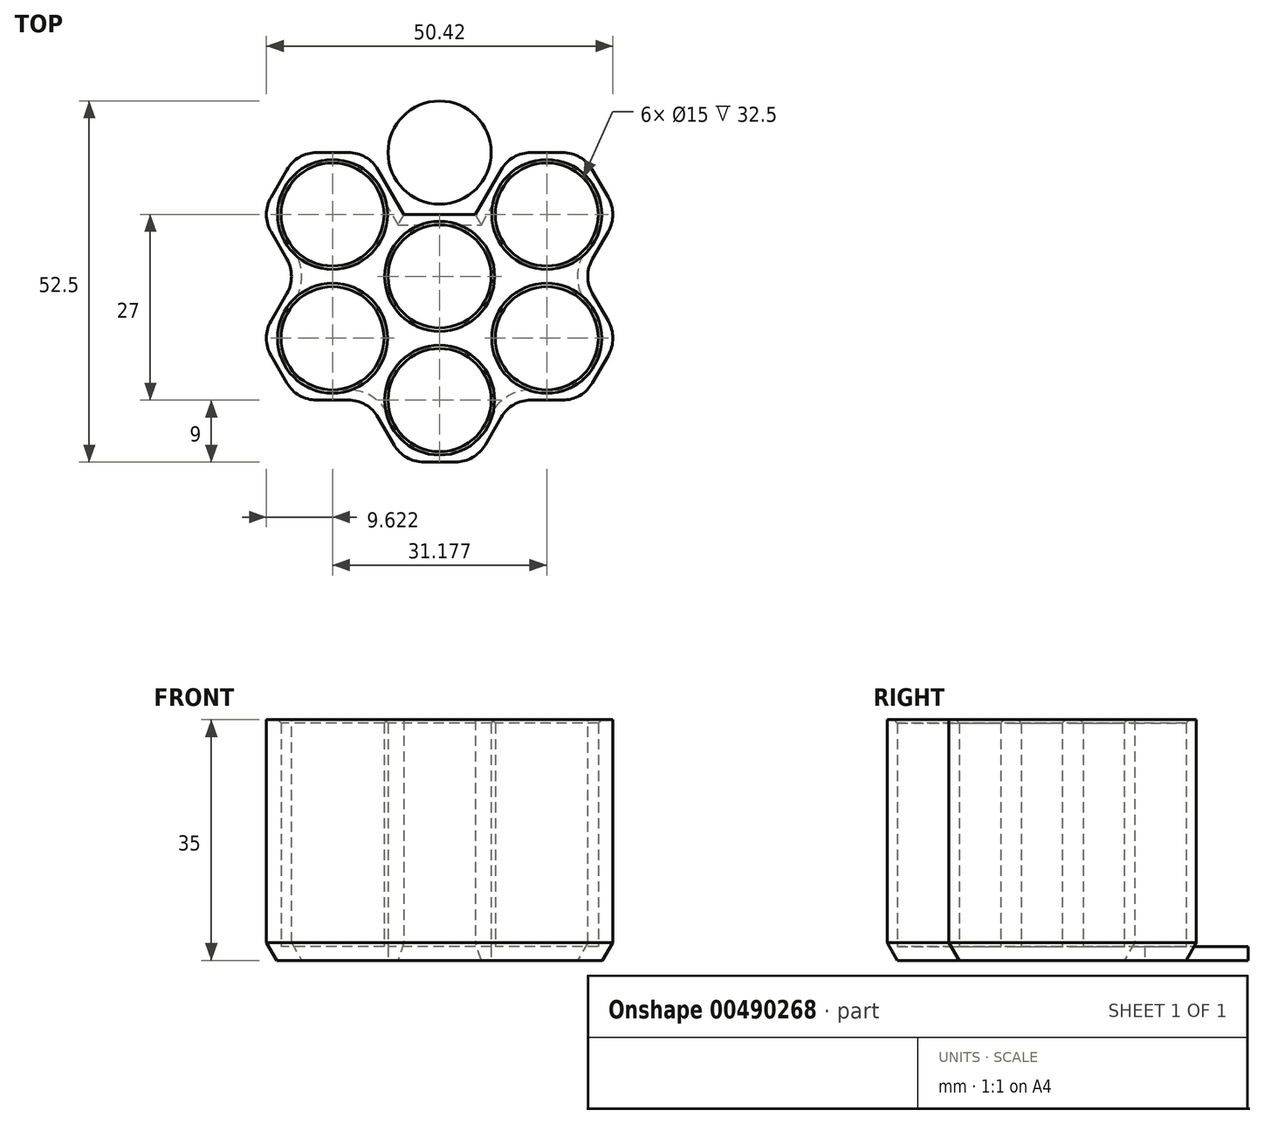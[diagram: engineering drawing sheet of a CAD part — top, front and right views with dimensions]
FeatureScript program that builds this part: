
annotation { "Feature Type Name" : "Feature", "Feature Type Description" : "" }
export const myFeature = defineFeature(function(context is Context, id is Id, definition is map)
    precondition{}
    {
        {
            var Q0;
            Q0=qCreatedBy(makeId("Top.planeOp"),FACE);
            var sketch = newSketch(context, id + "F0", { "sketchPlane" : qUnion([Q0])});
            skCircle(sketch, "E0", {"center": v(0, 0) * mm, "radius": 7.5 * mm});
            skCircle(sketch, "E1.cCircle", {"center": v(0, 0) * mm, "radius": 9 * mm, "construction": true});
            skLineSegment(sketch, "E1.0", {"start": v(-5.2, 9) * mm, "end": v(5.2, 9) * mm});
            skLineSegment(sketch, "E1.1", {"start": v(5.2, 9) * mm, "end": v(10.4, 0) * mm});
            skLineSegment(sketch, "E1.2", {"start": v(10.4, 0) * mm, "end": v(5.2, -9) * mm});
            skLineSegment(sketch, "E1.3", {"start": v(5.2, -9) * mm, "end": v(-5.2, -9) * mm});
            skLineSegment(sketch, "E1.4", {"start": v(-5.2, -9) * mm, "end": v(-10.4, 0) * mm});
            skLineSegment(sketch, "E1.5", {"start": v(-10.4, 0) * mm, "end": v(-5.2, 9) * mm});
            skPoint(sketch, "E1.0.midPoint", {"position": v(0, 9) * mm});
            skCircle(sketch, "E2.cCircle", {"center": v(0, 18) * mm, "radius": 9 * mm, "construction": true});
            skLineSegment(sketch, "E2.0", {"start": v(5.2, 9) * mm, "end": v(-5.2, 9) * mm});
            skLineSegment(sketch, "E2.1", {"start": v(-5.2, 9) * mm, "end": v(-10.4, 18) * mm});
            skLineSegment(sketch, "E2.2", {"start": v(-10.4, 18) * mm, "end": v(-5.2, 27) * mm});
            skLineSegment(sketch, "E2.3", {"start": v(-5.2, 27) * mm, "end": v(5.2, 27) * mm});
            skLineSegment(sketch, "E2.4", {"start": v(5.2, 27) * mm, "end": v(10.4, 18) * mm});
            skLineSegment(sketch, "E2.5", {"start": v(10.4, 18) * mm, "end": v(5.2, 9) * mm});
            skLineSegment(sketch, "E3.1.0", {"start": v(-25.98, 9) * mm, "end": v(-20.78, 18) * mm});
            skLineSegment(sketch, "E3.1.1", {"start": v(-20.78, 18) * mm, "end": v(-10.4, 18) * mm});
            skLineSegment(sketch, "E3.1.2", {"start": v(-10.4, 18) * mm, "end": v(-5.2, 9) * mm});
            skLineSegment(sketch, "E3.1.3", {"start": v(-10.4, 0) * mm, "end": v(-20.78, 0) * mm});
            skLineSegment(sketch, "E3.1.4", {"start": v(-20.78, 0) * mm, "end": v(-25.98, 9) * mm});
            skLineSegment(sketch, "E3.2.0", {"start": v(-20.78, -18) * mm, "end": v(-25.98, -9) * mm});
            skLineSegment(sketch, "E3.2.1", {"start": v(-25.98, -9) * mm, "end": v(-20.78, 0) * mm});
            skLineSegment(sketch, "E3.2.2", {"start": v(-20.78, 0) * mm, "end": v(-10.4, 0) * mm});
            skLineSegment(sketch, "E3.2.3", {"start": v(-5.2, -9) * mm, "end": v(-10.4, -18) * mm});
            skLineSegment(sketch, "E3.2.4", {"start": v(-10.4, -18) * mm, "end": v(-20.78, -18) * mm});
            skLineSegment(sketch, "E3.3.0", {"start": v(5.2, -27) * mm, "end": v(-5.2, -27) * mm});
            skLineSegment(sketch, "E3.3.1", {"start": v(-5.2, -27) * mm, "end": v(-10.4, -18) * mm});
            skLineSegment(sketch, "E3.3.2", {"start": v(-10.4, -18) * mm, "end": v(-5.2, -9) * mm});
            skLineSegment(sketch, "E3.3.3", {"start": v(5.2, -9) * mm, "end": v(10.4, -18) * mm});
            skLineSegment(sketch, "E3.3.4", {"start": v(10.4, -18) * mm, "end": v(5.2, -27) * mm});
            skLineSegment(sketch, "E3.4.0", {"start": v(25.98, -9) * mm, "end": v(20.78, -18) * mm});
            skLineSegment(sketch, "E3.4.1", {"start": v(20.78, -18) * mm, "end": v(10.4, -18) * mm});
            skLineSegment(sketch, "E3.4.2", {"start": v(10.4, -18) * mm, "end": v(5.2, -9) * mm});
            skLineSegment(sketch, "E3.4.3", {"start": v(10.4, 0) * mm, "end": v(20.78, 0) * mm});
            skLineSegment(sketch, "E3.4.4", {"start": v(20.78, 0) * mm, "end": v(25.98, -9) * mm});
            skLineSegment(sketch, "E3.5.0", {"start": v(20.78, 18) * mm, "end": v(25.98, 9) * mm});
            skLineSegment(sketch, "E3.5.1", {"start": v(25.98, 9) * mm, "end": v(20.78, 0) * mm});
            skLineSegment(sketch, "E3.5.2", {"start": v(20.78, 0) * mm, "end": v(10.4, 0) * mm});
            skLineSegment(sketch, "E3.5.3", {"start": v(5.2, 9) * mm, "end": v(10.4, 18) * mm});
            skLineSegment(sketch, "E3.5.4", {"start": v(10.4, 18) * mm, "end": v(20.78, 18) * mm});
            skCircle(sketch, "E4", {"center": v(0, 18) * mm, "radius": 7.5 * mm});
            skCircle(sketch, "E5.1.0", {"center": v(-15.59, 9) * mm, "radius": 7.5 * mm});
            skCircle(sketch, "E5.2.0", {"center": v(-15.59, -9) * mm, "radius": 7.5 * mm});
            skCircle(sketch, "E5.3.0", {"center": v(0, -18) * mm, "radius": 7.5 * mm});
            skCircle(sketch, "E5.4.0", {"center": v(15.59, -9) * mm, "radius": 7.5 * mm});
            skCircle(sketch, "E5.5.0", {"center": v(15.59, 9) * mm, "radius": 7.5 * mm});
            skSolve(sketch);
        }
        {
            var Q0;
            Q0=makeQuery(id+"F0.imprint","IMPRINT",FACE,{"disambiguationData":[TD([[makeQuery(id+"F0.imprint","IMPRINT",EDGE,{"derivedFrom":sQuery(id+"F0.wireOp",EDGE,"E1.5")}),1.0]])]});
            var Q1;
            Q1=makeQuery(id+"F0.imprint","IMPRINT",FACE,{"disambiguationData":[TD([[makeQuery(id+"F0.imprint","IMPRINT",EDGE,{"derivedFrom":sQuery(id+"F0.wireOp",EDGE,"E2.0")}),-1.0]])]});
            var Q2;
            Q2=makeQuery(id+"F0.imprint","IMPRINT",FACE,{"disambiguationData":[TD([[makeQuery(id+"F0.imprint","IMPRINT",EDGE,{"derivedFrom":sQuery(id+"F0.wireOp",EDGE,"E1.1")}),1.0]])]});
            var Q3;
            Q3=makeQuery(id+"F0.imprint","IMPRINT",FACE,{"disambiguationData":[TD([[makeQuery(id+"F0.imprint","IMPRINT",EDGE,{"derivedFrom":sQuery(id+"F0.wireOp",EDGE,"E0")}),-1.0]])]});
            var Q4;
            Q4=makeQuery(id+"F0.imprint","IMPRINT",FACE,{"disambiguationData":[TD([[makeQuery(id+"F0.imprint","IMPRINT",EDGE,{"derivedFrom":sQuery(id+"F0.wireOp",EDGE,"E1.2")}),1.0]])]});
            var Q5;
            Q5=makeQuery(id+"F0.imprint","IMPRINT",FACE,{"disambiguationData":[TD([[makeQuery(id+"F0.imprint","IMPRINT",EDGE,{"derivedFrom":sQuery(id+"F0.wireOp",EDGE,"E1.3")}),1.0]])]});
            var Q6;
            Q6=makeQuery(id+"F0.imprint","IMPRINT",FACE,{"disambiguationData":[TD([[makeQuery(id+"F0.imprint","IMPRINT",EDGE,{"derivedFrom":sQuery(id+"F0.wireOp",EDGE,"E1.4")}),1.0]])]});
            extrude(context, id + "F1", {"entities" : qUnion([Q0, Q1, Q2, Q3, Q4, Q5, Q6]), "depth" : 35 * mm});
        }
        {
            var Q0;
            Q0=makeQuery(id+"F0.imprint","IMPRINT",FACE,{"disambiguationData":[TD([[makeQuery(id+"F0.imprint","IMPRINT",EDGE,{"derivedFrom":sQuery(id+"F0.wireOp",EDGE,"E5.1.0")}),1.0]])]});
            var Q1;
            Q1=makeQuery(id+"F0.imprint","IMPRINT",FACE,{"disambiguationData":[TD([[makeQuery(id+"F0.imprint","IMPRINT",EDGE,{"derivedFrom":sQuery(id+"F0.wireOp",EDGE,"E5.2.0")}),1.0]])]});
            var Q2;
            Q2=makeQuery(id+"F0.imprint","IMPRINT",FACE,{"disambiguationData":[TD([[makeQuery(id+"F0.imprint","IMPRINT",EDGE,{"derivedFrom":sQuery(id+"F0.wireOp",EDGE,"E4")}),1.0]])]});
            var Q3;
            Q3=makeQuery(id+"F0.imprint","IMPRINT",FACE,{"disambiguationData":[TD([[makeQuery(id+"F0.imprint","IMPRINT",EDGE,{"derivedFrom":sQuery(id+"F0.wireOp",EDGE,"E0")}),1.0]])]});
            var Q4;
            Q4=makeQuery(id+"F0.imprint","IMPRINT",FACE,{"disambiguationData":[TD([[makeQuery(id+"F0.imprint","IMPRINT",EDGE,{"derivedFrom":sQuery(id+"F0.wireOp",EDGE,"E5.5.0")}),1.0]])]});
            var Q5;
            Q5=makeQuery(id+"F0.imprint","IMPRINT",FACE,{"disambiguationData":[TD([[makeQuery(id+"F0.imprint","IMPRINT",EDGE,{"derivedFrom":sQuery(id+"F0.wireOp",EDGE,"E5.4.0")}),1.0]])]});
            var Q6;
            Q6=makeQuery(id+"F0.imprint","IMPRINT",FACE,{"disambiguationData":[TD([[makeQuery(id+"F0.imprint","IMPRINT",EDGE,{"derivedFrom":sQuery(id+"F0.wireOp",EDGE,"E5.3.0")}),1.0]])]});
            extrude(context, id + "F2", {"entities" : qUnion([Q0, Q1, Q2, Q3, Q4, Q5, Q6]), "operationType" : NewBodyOperationType.ADD, "depth" : 2 * mm});
        }
        {
            var Q0;
            Q0=makeQuery(id+"F1.opExtrude","CAP_EDGE",EDGE,{"disambiguationData":[OSD([sQuery(id+"F0.wireOp",EDGE,"E4")])],"isStart":false});
            var Q1;
            Q1=makeQuery(id+"F1.opExtrude","CAP_EDGE",EDGE,{"disambiguationData":[OSD([sQuery(id+"F0.wireOp",EDGE,"E5.1.0")])],"isStart":false});
            var Q2;
            Q2=makeQuery(id+"F1.opExtrude","CAP_EDGE",EDGE,{"disambiguationData":[OSD([sQuery(id+"F0.wireOp",EDGE,"E0")])],"isStart":false});
            var Q3;
            Q3=makeQuery(id+"F1.opExtrude","CAP_EDGE",EDGE,{"disambiguationData":[OSD([sQuery(id+"F0.wireOp",EDGE,"E5.2.0")])],"isStart":false});
            var Q4;
            Q4=makeQuery(id+"F1.opExtrude","CAP_EDGE",EDGE,{"disambiguationData":[OSD([sQuery(id+"F0.wireOp",EDGE,"E5.5.0")])],"isStart":false});
            var Q5;
            Q5=makeQuery(id+"F1.opExtrude","CAP_EDGE",EDGE,{"disambiguationData":[OSD([sQuery(id+"F0.wireOp",EDGE,"E5.4.0")])],"isStart":false});
            var Q6;
            Q6=makeQuery(id+"F1.opExtrude","CAP_EDGE",EDGE,{"disambiguationData":[OSD([sQuery(id+"F0.wireOp",EDGE,"E5.3.0")])],"isStart":false});
            chamfer(context, id + "F3", {"entities" : qUnion([Q0, Q1, Q2, Q3, Q4, Q5, Q6]), "width" : .5 * mm, "tangentPropagation" : true});
        }
        {
            var Q0;
            Q0=makeQuery(id+"F1.opExtrude","SWEPT_EDGE",EDGE,{"disambiguationData":[OSD([sQuery(id+"F0.wireOp",EDGE,"E3.1.0"),sQuery(id+"F0.wireOp",EDGE,"E3.1.4")])]});
            var Q1;
            Q1=makeQuery(id+"F1.opExtrude","SWEPT_EDGE",EDGE,{"disambiguationData":[OSD([sQuery(id+"F0.wireOp",EDGE,"E3.1.0"),sQuery(id+"F0.wireOp",EDGE,"E3.1.1")])]});
            var Q2;
            Q2=makeQuery(id+"F1.opExtrude","SWEPT_EDGE",EDGE,{"disambiguationData":[OSD([sQuery(id+"F0.wireOp",EDGE,"E2.2"),sQuery(id+"F0.wireOp",EDGE,"E3.1.1"),sQuery(id+"F0.wireOp",EDGE,"E3.1.2")])]});
            var Q3;
            Q3=makeQuery(id+"F1.opExtrude","SWEPT_EDGE",EDGE,{"disambiguationData":[OSD([sQuery(id+"F0.wireOp",EDGE,"E2.2"),sQuery(id+"F0.wireOp",EDGE,"E2.3")])]});
            var Q4;
            Q4=makeQuery(id+"F1.opExtrude","SWEPT_EDGE",EDGE,{"disambiguationData":[OSD([sQuery(id+"F0.wireOp",EDGE,"E2.3"),sQuery(id+"F0.wireOp",EDGE,"E2.4")])]});
            var Q5;
            Q5=makeQuery(id+"F1.opExtrude","SWEPT_EDGE",EDGE,{"disambiguationData":[OSD([sQuery(id+"F0.wireOp",EDGE,"E2.4"),sQuery(id+"F0.wireOp",EDGE,"E3.5.3"),sQuery(id+"F0.wireOp",EDGE,"E3.5.4")])]});
            var Q6;
            Q6=makeQuery(id+"F1.opExtrude","SWEPT_EDGE",EDGE,{"disambiguationData":[OSD([sQuery(id+"F0.wireOp",EDGE,"E3.5.0"),sQuery(id+"F0.wireOp",EDGE,"E3.5.4")])]});
            var Q7;
            Q7=makeQuery(id+"F1.opExtrude","SWEPT_EDGE",EDGE,{"disambiguationData":[OSD([sQuery(id+"F0.wireOp",EDGE,"E3.5.0"),sQuery(id+"F0.wireOp",EDGE,"E3.5.1")])]});
            var Q8;
            Q8=makeQuery(id+"F1.opExtrude","SWEPT_EDGE",EDGE,{"disambiguationData":[OSD([sQuery(id+"F0.wireOp",EDGE,"E3.4.4"),sQuery(id+"F0.wireOp",EDGE,"E3.5.1"),sQuery(id+"F0.wireOp",EDGE,"E3.5.2")])]});
            var Q9;
            Q9=makeQuery(id+"F1.opExtrude","SWEPT_EDGE",EDGE,{"disambiguationData":[OSD([sQuery(id+"F0.wireOp",EDGE,"E3.4.0"),sQuery(id+"F0.wireOp",EDGE,"E3.4.4")])]});
            var Q10;
            Q10=makeQuery(id+"F1.opExtrude","SWEPT_EDGE",EDGE,{"disambiguationData":[OSD([sQuery(id+"F0.wireOp",EDGE,"E3.4.0"),sQuery(id+"F0.wireOp",EDGE,"E3.4.1")])]});
            var Q11;
            Q11=makeQuery(id+"F1.opExtrude","SWEPT_EDGE",EDGE,{"disambiguationData":[OSD([sQuery(id+"F0.wireOp",EDGE,"E3.3.4"),sQuery(id+"F0.wireOp",EDGE,"E3.4.1"),sQuery(id+"F0.wireOp",EDGE,"E3.4.2")])]});
            var Q12;
            Q12=makeQuery(id+"F1.opExtrude","SWEPT_EDGE",EDGE,{"disambiguationData":[OSD([sQuery(id+"F0.wireOp",EDGE,"E3.3.0"),sQuery(id+"F0.wireOp",EDGE,"E3.3.4")])]});
            var Q13;
            Q13=makeQuery(id+"F1.opExtrude","SWEPT_EDGE",EDGE,{"disambiguationData":[OSD([sQuery(id+"F0.wireOp",EDGE,"E3.3.0"),sQuery(id+"F0.wireOp",EDGE,"E3.3.1")])]});
            var Q14;
            Q14=makeQuery(id+"F1.opExtrude","SWEPT_EDGE",EDGE,{"disambiguationData":[OSD([sQuery(id+"F0.wireOp",EDGE,"E3.2.4"),sQuery(id+"F0.wireOp",EDGE,"E3.3.1"),sQuery(id+"F0.wireOp",EDGE,"E3.3.2")])]});
            var Q15;
            Q15=makeQuery(id+"F1.opExtrude","SWEPT_EDGE",EDGE,{"disambiguationData":[OSD([sQuery(id+"F0.wireOp",EDGE,"E3.2.0"),sQuery(id+"F0.wireOp",EDGE,"E3.2.4")])]});
            var Q16;
            Q16=makeQuery(id+"F1.opExtrude","SWEPT_EDGE",EDGE,{"disambiguationData":[OSD([sQuery(id+"F0.wireOp",EDGE,"E3.2.0"),sQuery(id+"F0.wireOp",EDGE,"E3.2.1")])]});
            var Q17;
            Q17=makeQuery(id+"F1.opExtrude","SWEPT_EDGE",EDGE,{"disambiguationData":[OSD([sQuery(id+"F0.wireOp",EDGE,"E3.1.4"),sQuery(id+"F0.wireOp",EDGE,"E3.2.1"),sQuery(id+"F0.wireOp",EDGE,"E3.2.2")])]});
            fillet(context, id + "F4", {"entities" : qUnion([Q0, Q1, Q2, Q3, Q4, Q5, Q6, Q7, Q8, Q9, Q10, Q11, Q12, Q13, Q14, Q15, Q16, Q17]), "radius" : 5 * mm, "tangentPropagation" : true, "allowEdgeOverflow" : false});
        }
        {
            var Q0;
            {var subQ0=sQuery(id+"F0.wireOp",EDGE,"E5.5.0");var subQ1=sQuery(id+"F0.wireOp",EDGE,"E5.4.0");var subQ2=sQuery(id+"F0.wireOp",EDGE,"E5.3.0");var subQ3=sQuery(id+"F0.wireOp",EDGE,"E5.2.0");var subQ4=sQuery(id+"F0.wireOp",EDGE,"E5.1.0");var subQ5=sQuery(id+"F0.wireOp",EDGE,"E4");var subQ6=sQuery(id+"F0.wireOp",EDGE,"E0");Q0=makeQuery(id+"F2.boolean.opBoolean","MERGE",FACE,{"derivedFrom":[makeQuery(id+"F1.opExtrude","CAP_FACE",FACE,{"disambiguationData":[OSD([subQ6,sQuery(id+"F0.wireOp",EDGE,"E2.2"),sQuery(id+"F0.wireOp",EDGE,"E2.3"),sQuery(id+"F0.wireOp",EDGE,"E2.4"),sQuery(id+"F0.wireOp",EDGE,"E3.1.0"),sQuery(id+"F0.wireOp",EDGE,"E3.1.1"),sQuery(id+"F0.wireOp",EDGE,"E3.1.4"),sQuery(id+"F0.wireOp",EDGE,"E3.2.0"),sQuery(id+"F0.wireOp",EDGE,"E3.2.1"),sQuery(id+"F0.wireOp",EDGE,"E3.2.4"),sQuery(id+"F0.wireOp",EDGE,"E3.3.0"),sQuery(id+"F0.wireOp",EDGE,"E3.3.1"),sQuery(id+"F0.wireOp",EDGE,"E3.3.4"),sQuery(id+"F0.wireOp",EDGE,"E3.4.0"),sQuery(id+"F0.wireOp",EDGE,"E3.4.1"),sQuery(id+"F0.wireOp",EDGE,"E3.4.4"),sQuery(id+"F0.wireOp",EDGE,"E3.5.0"),sQuery(id+"F0.wireOp",EDGE,"E3.5.1"),sQuery(id+"F0.wireOp",EDGE,"E3.5.4"),subQ5,subQ4,subQ3,subQ2,subQ1,subQ0])],"isStart":true}),makeQuery(id+"F2.opExtrude","CAP_FACE",FACE,{"disambiguationData":[OSD([subQ6])],"isStart":true}),makeQuery(id+"F2.opExtrude","CAP_FACE",FACE,{"disambiguationData":[OSD([subQ5])],"isStart":true}),makeQuery(id+"F2.opExtrude","CAP_FACE",FACE,{"disambiguationData":[OSD([subQ4])],"isStart":true}),makeQuery(id+"F2.opExtrude","CAP_FACE",FACE,{"disambiguationData":[OSD([subQ3])],"isStart":true}),makeQuery(id+"F2.opExtrude","CAP_FACE",FACE,{"disambiguationData":[OSD([subQ2])],"isStart":true}),makeQuery(id+"F2.opExtrude","CAP_FACE",FACE,{"disambiguationData":[OSD([subQ1])],"isStart":true}),makeQuery(id+"F2.opExtrude","CAP_FACE",FACE,{"disambiguationData":[OSD([subQ0])],"isStart":true})]});}
            chamfer(context, id + "F5", {"entities" : qUnion([Q0]), "chamferType" : ChamferType.OFFSET_ANGLE, "width" : 1.5 * mm, "oppositeDirection" : false, "angle" : 60 * degree, "tangentPropagation" : true});
        }
    });
